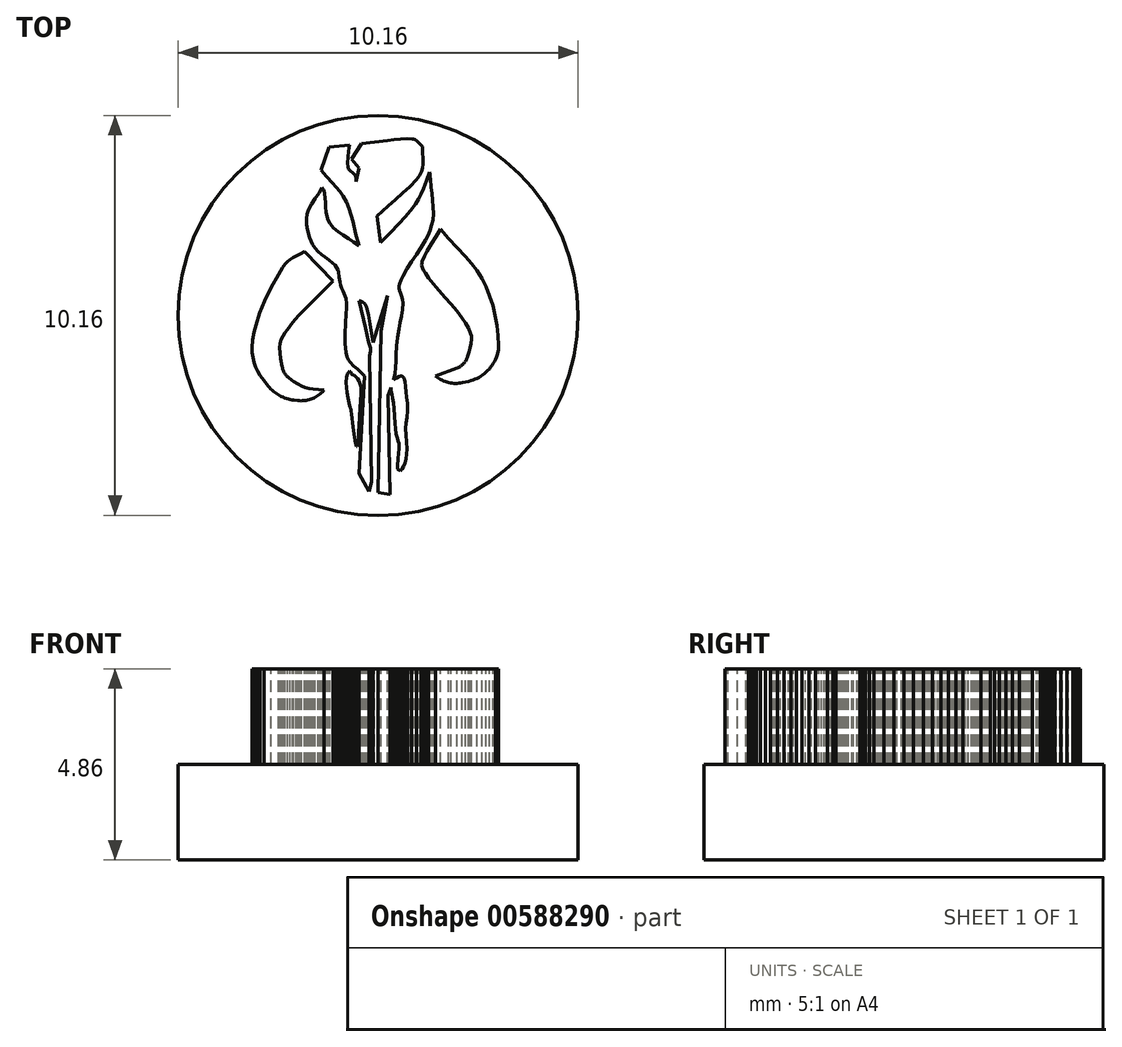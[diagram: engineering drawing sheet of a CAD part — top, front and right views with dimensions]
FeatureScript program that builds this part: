
annotation { "Feature Type Name" : "Feature", "Feature Type Description" : "" }
export const myFeature = defineFeature(function(context is Context, id is Id, definition is map)
    precondition{}
    {
        {
            var Q0;
            Q0=qCreatedBy(makeId("Top.planeOp"),FACE);
            var sketch = newSketch(context, id + "F0", { "sketchPlane" : qUnion([Q0])});
            skLineSegment(sketch, "E0", {"start": v(-3.17, -5.44) * mm, "end": v(-3.05, -5.48) * mm});
            skLineSegment(sketch, "E1", {"start": v(-3.05, -5.48) * mm, "end": v(-3, -5.51) * mm});
            skLineSegment(sketch, "E2", {"start": v(-3, -5.51) * mm, "end": v(-2.97, -5.54) * mm});
            skLineSegment(sketch, "E3", {"start": v(-2.97, -5.54) * mm, "end": v(-2.94, -5.6) * mm});
            skLineSegment(sketch, "E4", {"start": v(-2.94, -5.6) * mm, "end": v(-2.93, -5.66) * mm});
            skLineSegment(sketch, "E5", {"start": v(-2.93, -5.66) * mm, "end": v(-2.91, -5.76) * mm});
            skLineSegment(sketch, "E6", {"start": v(-2.91, -5.76) * mm, "end": v(-2.89, -5.81) * mm});
            skLineSegment(sketch, "E7", {"start": v(-2.89, -5.81) * mm, "end": v(-2.85, -5.86) * mm});
            skLineSegment(sketch, "E8", {"start": v(-2.85, -5.86) * mm, "end": v(-2.75, -5.91) * mm});
            skLineSegment(sketch, "E9", {"start": v(-2.75, -5.91) * mm, "end": v(-2.55, -5.98) * mm});
            skLineSegment(sketch, "E10", {"start": v(-2.55, -5.98) * mm, "end": v(-2.5, -6.01) * mm});
            skLineSegment(sketch, "E11", {"start": v(-2.5, -6.01) * mm, "end": v(-2.48, -6.03) * mm});
            skLineSegment(sketch, "E12", {"start": v(-2.48, -6.03) * mm, "end": v(-2.48, -6.03) * mm});
            skLineSegment(sketch, "E13", {"start": v(-2.48, -6.03) * mm, "end": v(-2.47, -6.04) * mm});
            skLineSegment(sketch, "E14", {"start": v(-2.47, -6.04) * mm, "end": v(-2.46, -6.05) * mm});
            skLineSegment(sketch, "E15", {"start": v(-2.46, -6.05) * mm, "end": v(-2.42, -6.08) * mm});
            skLineSegment(sketch, "E16", {"start": v(-2.42, -6.08) * mm, "end": v(-2.27, -6.23) * mm});
            skLineSegment(sketch, "E17", {"start": v(-2.27, -6.23) * mm, "end": v(-2, -6.56) * mm});
            skLineSegment(sketch, "E18", {"start": v(-2, -6.56) * mm, "end": v(-1.76, -6.92) * mm});
            skLineSegment(sketch, "E19", {"start": v(-1.76, -6.92) * mm, "end": v(-1.59, -7.32) * mm});
            skLineSegment(sketch, "E20", {"start": v(-1.59, -7.32) * mm, "end": v(-1.5, -7.74) * mm});
            skLineSegment(sketch, "E21", {"start": v(-1.5, -7.74) * mm, "end": v(-1.46, -8.75) * mm});
            skLineSegment(sketch, "E22", {"start": v(-1.46, -8.75) * mm, "end": v(-1.5, -9.75) * mm});
            skLineSegment(sketch, "E23", {"start": v(-1.5, -9.75) * mm, "end": v(-1.58, -10.76) * mm});
            skLineSegment(sketch, "E24", {"start": v(-1.58, -10.76) * mm, "end": v(-1.78, -13.47) * mm});
            skLineSegment(sketch, "E25", {"start": v(-1.78, -13.47) * mm, "end": v(-1.82, -14.2) * mm});
            skLineSegment(sketch, "E26", {"start": v(-1.82, -14.2) * mm, "end": v(-1.82, -14.94) * mm});
            skLineSegment(sketch, "E27", {"start": v(-1.82, -14.94) * mm, "end": v(-1.85, -15.67) * mm});
            skLineSegment(sketch, "E28", {"start": v(-1.85, -15.67) * mm, "end": v(-1.94, -16.21) * mm});
            skLineSegment(sketch, "E29", {"start": v(-1.94, -16.21) * mm, "end": v(-1.97, -16.33) * mm});
            skLineSegment(sketch, "E30", {"start": v(-1.97, -16.33) * mm, "end": v(-2.02, -16.45) * mm});
            skLineSegment(sketch, "E31", {"start": v(-2.02, -16.45) * mm, "end": v(-2.04, -16.47) * mm});
            skLineSegment(sketch, "E32", {"start": v(-2.04, -16.47) * mm, "end": v(-2.05, -16.47) * mm});
            skLineSegment(sketch, "E33", {"start": v(-2.05, -16.47) * mm, "end": v(-2.06, -16.47) * mm});
            skLineSegment(sketch, "E34", {"start": v(-2.06, -16.47) * mm, "end": v(-2.08, -16.47) * mm});
            skLineSegment(sketch, "E35", {"start": v(-2.08, -16.47) * mm, "end": v(-2.1, -16.46) * mm});
            skLineSegment(sketch, "E36", {"start": v(-2.1, -16.46) * mm, "end": v(-2.12, -16.43) * mm});
            skLineSegment(sketch, "E37", {"start": v(-2.12, -16.43) * mm, "end": v(-2.2, -16.26) * mm});
            skLineSegment(sketch, "E38", {"start": v(-2.2, -16.26) * mm, "end": v(-2.3, -15.9) * mm});
            skLineSegment(sketch, "E39", {"start": v(-2.3, -15.9) * mm, "end": v(-2.38, -15.55) * mm});
            skLineSegment(sketch, "E40", {"start": v(-2.38, -15.55) * mm, "end": v(-2.52, -14.6) * mm});
            skLineSegment(sketch, "E41", {"start": v(-2.52, -14.6) * mm, "end": v(-2.63, -13.64) * mm});
            skLineSegment(sketch, "E42", {"start": v(-2.63, -13.64) * mm, "end": v(-2.86, -11.73) * mm});
            skLineSegment(sketch, "E43", {"start": v(-2.86, -11.73) * mm, "end": v(-2.92, -11.25) * mm});
            skLineSegment(sketch, "E44", {"start": v(-2.92, -11.25) * mm, "end": v(-2.95, -11.02) * mm});
            skLineSegment(sketch, "E45", {"start": v(-2.95, -11.02) * mm, "end": v(-2.97, -10.9) * mm});
            skLineSegment(sketch, "E46", {"start": v(-2.97, -10.9) * mm, "end": v(-2.98, -10.88) * mm});
            skLineSegment(sketch, "E47", {"start": v(-2.98, -10.88) * mm, "end": v(-2.98, -10.87) * mm});
            skLineSegment(sketch, "E48", {"start": v(-2.98, -10.87) * mm, "end": v(-3.03, -10.84) * mm});
            skLineSegment(sketch, "E49", {"start": v(-3.03, -10.84) * mm, "end": v(-3.05, -10.82) * mm});
            skLineSegment(sketch, "E50", {"start": v(-3.05, -10.82) * mm, "end": v(-3.07, -10.8) * mm});
            skLineSegment(sketch, "E51", {"start": v(-3.07, -10.8) * mm, "end": v(-3.07, -10.8) * mm});
            skLineSegment(sketch, "E52", {"start": v(-3.07, -10.8) * mm, "end": v(-3.07, -10.77) * mm});
            skLineSegment(sketch, "E53", {"start": v(-3.07, -10.77) * mm, "end": v(-3.09, -10.7) * mm});
            skLineSegment(sketch, "E54", {"start": v(-3.09, -10.7) * mm, "end": v(-3.15, -10.43) * mm});
            skLineSegment(sketch, "E55", {"start": v(-3.15, -10.43) * mm, "end": v(-3.37, -9.34) * mm});
            skLineSegment(sketch, "E56", {"start": v(-3.37, -9.34) * mm, "end": v(-3.5, -8.6) * mm});
            skLineSegment(sketch, "E57", {"start": v(-3.5, -8.6) * mm, "end": v(-3.59, -7.84) * mm});
            skLineSegment(sketch, "E58", {"start": v(-3.59, -7.84) * mm, "end": v(-3.63, -7.09) * mm});
            skLineSegment(sketch, "E59", {"start": v(-3.63, -7.09) * mm, "end": v(-3.57, -6.34) * mm});
            skLineSegment(sketch, "E60", {"start": v(-3.57, -6.34) * mm, "end": v(-3.5, -6.07) * mm});
            skLineSegment(sketch, "E61", {"start": v(-3.5, -6.07) * mm, "end": v(-3.42, -5.81) * mm});
            skLineSegment(sketch, "E62", {"start": v(-3.42, -5.81) * mm, "end": v(-3.3, -5.61) * mm});
            skLineSegment(sketch, "E63", {"start": v(-3.3, -5.61) * mm, "end": v(-3.17, -5.44) * mm});
            skLineSegment(sketch, "E64", {"start": v(8.53, 23.62) * mm, "end": v(8.6, 23.33) * mm});
            skLineSegment(sketch, "E65", {"start": v(8.6, 23.33) * mm, "end": v(8.62, 23.18) * mm});
            skLineSegment(sketch, "E66", {"start": v(8.62, 23.18) * mm, "end": v(8.63, 23.03) * mm});
            skLineSegment(sketch, "E67", {"start": v(8.63, 23.03) * mm, "end": v(8.63, 23.03) * mm});
            skLineSegment(sketch, "E68", {"start": v(8.63, 23.03) * mm, "end": v(8.63, 23) * mm});
            skLineSegment(sketch, "E69", {"start": v(8.63, 23) * mm, "end": v(8.64, 22.93) * mm});
            skLineSegment(sketch, "E70", {"start": v(8.64, 22.93) * mm, "end": v(8.65, 22.63) * mm});
            skLineSegment(sketch, "E71", {"start": v(8.65, 22.63) * mm, "end": v(8.77, 21.44) * mm});
            skLineSegment(sketch, "E72", {"start": v(8.77, 21.44) * mm, "end": v(8.89, 20.48) * mm});
            skLineSegment(sketch, "E73", {"start": v(8.89, 20.48) * mm, "end": v(9, 19.52) * mm});
            skLineSegment(sketch, "E74", {"start": v(9, 19.52) * mm, "end": v(9.08, 18.56) * mm});
            skLineSegment(sketch, "E75", {"start": v(9.08, 18.56) * mm, "end": v(9.1, 17.6) * mm});
            skLineSegment(sketch, "E76", {"start": v(9.1, 17.6) * mm, "end": v(9.01, 16.64) * mm});
            skLineSegment(sketch, "E77", {"start": v(9.01, 16.64) * mm, "end": v(8.85, 15.87) * mm});
            skLineSegment(sketch, "E78", {"start": v(8.85, 15.87) * mm, "end": v(8.6, 15.12) * mm});
            skLineSegment(sketch, "E79", {"start": v(8.6, 15.12) * mm, "end": v(8.3, 14.38) * mm});
            skLineSegment(sketch, "E80", {"start": v(8.3, 14.38) * mm, "end": v(7.94, 13.68) * mm});
            skLineSegment(sketch, "E81", {"start": v(7.94, 13.68) * mm, "end": v(7.3, 12.62) * mm});
            skLineSegment(sketch, "E82", {"start": v(7.3, 12.62) * mm, "end": v(6.62, 11.6) * mm});
            skLineSegment(sketch, "E83", {"start": v(6.62, 11.6) * mm, "end": v(5.92, 10.57) * mm});
            skLineSegment(sketch, "E84", {"start": v(5.92, 10.57) * mm, "end": v(5.25, 9.53) * mm});
            skLineSegment(sketch, "E85", {"start": v(5.25, 9.53) * mm, "end": v(4.65, 8.45) * mm});
            skLineSegment(sketch, "E86", {"start": v(4.65, 8.45) * mm, "end": v(4.36, 7.86) * mm});
            skLineSegment(sketch, "E87", {"start": v(4.36, 7.86) * mm, "end": v(4.14, 7.24) * mm});
            skLineSegment(sketch, "E88", {"start": v(4.14, 7.24) * mm, "end": v(4.1, 6.96) * mm});
            skLineSegment(sketch, "E89", {"start": v(4.1, 6.96) * mm, "end": v(4.1, 6.68) * mm});
            skLineSegment(sketch, "E90", {"start": v(4.1, 6.68) * mm, "end": v(4.17, 6.31) * mm});
            skLineSegment(sketch, "E91", {"start": v(4.17, 6.31) * mm, "end": v(4.28, 5.96) * mm});
            skLineSegment(sketch, "E92", {"start": v(4.28, 5.96) * mm, "end": v(4.45, 5.49) * mm});
            skLineSegment(sketch, "E93", {"start": v(4.45, 5.49) * mm, "end": v(4.6, 5.02) * mm});
            skLineSegment(sketch, "E94", {"start": v(4.6, 5.02) * mm, "end": v(4.67, 4.53) * mm});
            skLineSegment(sketch, "E95", {"start": v(4.67, 4.53) * mm, "end": v(4.63, 3.56) * mm});
            skLineSegment(sketch, "E96", {"start": v(4.63, 3.56) * mm, "end": v(4.48, 2.6) * mm});
            skLineSegment(sketch, "E97", {"start": v(4.48, 2.6) * mm, "end": v(4.26, 1.63) * mm});
            skLineSegment(sketch, "E98", {"start": v(4.26, 1.63) * mm, "end": v(4.05, 0.68) * mm});
            skLineSegment(sketch, "E99", {"start": v(4.05, 0.68) * mm, "end": v(3.85, -0.55) * mm});
            skLineSegment(sketch, "E100", {"start": v(3.85, -0.55) * mm, "end": v(3.72, -1.78) * mm});
            skLineSegment(sketch, "E101", {"start": v(3.72, -1.78) * mm, "end": v(3.66, -3.03) * mm});
            skLineSegment(sketch, "E102", {"start": v(3.66, -3.03) * mm, "end": v(3.64, -3.96) * mm});
            skLineSegment(sketch, "E103", {"start": v(3.64, -3.96) * mm, "end": v(3.58, -4.9) * mm});
            skLineSegment(sketch, "E104", {"start": v(3.58, -4.9) * mm, "end": v(3.47, -5.82) * mm});
            skLineSegment(sketch, "E105", {"start": v(3.47, -5.82) * mm, "end": v(3.27, -6.73) * mm});
            skLineSegment(sketch, "E106", {"start": v(1.4, 13.3) * mm, "end": v(2.74, 14.74) * mm});
            skLineSegment(sketch, "E107", {"start": v(2.74, 14.74) * mm, "end": v(4.1, 16.14) * mm});
            skLineSegment(sketch, "E108", {"start": v(4.1, 16.14) * mm, "end": v(4.94, 17.05) * mm});
            skLineSegment(sketch, "E109", {"start": v(4.94, 17.05) * mm, "end": v(5.75, 18) * mm});
            skLineSegment(sketch, "E110", {"start": v(5.75, 18) * mm, "end": v(6.5, 18.98) * mm});
            skLineSegment(sketch, "E111", {"start": v(6.5, 18.98) * mm, "end": v(6.93, 19.69) * mm});
            skLineSegment(sketch, "E112", {"start": v(6.93, 19.69) * mm, "end": v(7.3, 20.44) * mm});
            skLineSegment(sketch, "E113", {"start": v(7.3, 20.44) * mm, "end": v(7.63, 21.22) * mm});
            skLineSegment(sketch, "E114", {"start": v(7.63, 21.22) * mm, "end": v(8.07, 22.43) * mm});
            skLineSegment(sketch, "E115", {"start": v(8.07, 22.43) * mm, "end": v(8.53, 23.62) * mm});
            skLineSegment(sketch, "E116", {"start": v(0.9, 17.17) * mm, "end": v(1.4, 13.3) * mm});
            skLineSegment(sketch, "E117", {"start": v(7.54, 27.39) * mm, "end": v(7.55, 26.52) * mm});
            skLineSegment(sketch, "E118", {"start": v(7.55, 26.52) * mm, "end": v(7.6, 25.64) * mm});
            skLineSegment(sketch, "E119", {"start": v(7.6, 25.64) * mm, "end": v(7.61, 24.77) * mm});
            skLineSegment(sketch, "E120", {"start": v(7.61, 24.77) * mm, "end": v(7.54, 24.23) * mm});
            skLineSegment(sketch, "E121", {"start": v(7.54, 24.23) * mm, "end": v(7.39, 23.72) * mm});
            skLineSegment(sketch, "E122", {"start": v(7.39, 23.72) * mm, "end": v(7.06, 23.12) * mm});
            skLineSegment(sketch, "E123", {"start": v(7.06, 23.12) * mm, "end": v(6.65, 22.57) * mm});
            skLineSegment(sketch, "E124", {"start": v(6.65, 22.57) * mm, "end": v(5.67, 21.53) * mm});
            skLineSegment(sketch, "E125", {"start": v(5.67, 21.53) * mm, "end": v(4.63, 20.55) * mm});
            skLineSegment(sketch, "E126", {"start": v(4.63, 20.55) * mm, "end": v(3.55, 19.6) * mm});
            skLineSegment(sketch, "E127", {"start": v(3.55, 19.6) * mm, "end": v(2.48, 18.64) * mm});
            skLineSegment(sketch, "E128", {"start": v(2.48, 18.64) * mm, "end": v(0.9, 17.17) * mm});
            skLineSegment(sketch, "E129", {"start": v(-1.38, 27.79) * mm, "end": v(0.5, 28.01) * mm});
            skLineSegment(sketch, "E130", {"start": v(0.5, 28.01) * mm, "end": v(2.4, 28.27) * mm});
            skLineSegment(sketch, "E131", {"start": v(2.4, 28.27) * mm, "end": v(3.34, 28.38) * mm});
            skLineSegment(sketch, "E132", {"start": v(3.34, 28.38) * mm, "end": v(4.29, 28.46) * mm});
            skLineSegment(sketch, "E133", {"start": v(4.29, 28.46) * mm, "end": v(5.23, 28.5) * mm});
            skLineSegment(sketch, "E134", {"start": v(5.23, 28.5) * mm, "end": v(5.99, 28.48) * mm});
            skLineSegment(sketch, "E135", {"start": v(5.99, 28.48) * mm, "end": v(6.2, 28.46) * mm});
            skLineSegment(sketch, "E136", {"start": v(6.2, 28.46) * mm, "end": v(6.39, 28.4) * mm});
            skLineSegment(sketch, "E137", {"start": v(6.39, 28.4) * mm, "end": v(6.6, 28.26) * mm});
            skLineSegment(sketch, "E138", {"start": v(6.6, 28.26) * mm, "end": v(6.8, 28.1) * mm});
            skLineSegment(sketch, "E139", {"start": v(6.8, 28.1) * mm, "end": v(7.16, 27.73) * mm});
            skLineSegment(sketch, "E140", {"start": v(7.16, 27.73) * mm, "end": v(7.54, 27.39) * mm});
            skLineSegment(sketch, "E141", {"start": v(-2.87, 25.5) * mm, "end": v(-1.38, 27.79) * mm});
            skLineSegment(sketch, "E142", {"start": v(-1.78, 24.22) * mm, "end": v(-2.87, 25.5) * mm});
            skLineSegment(sketch, "E143", {"start": v(-2.18, 22.23) * mm, "end": v(-1.78, 24.22) * mm});
            skLineSegment(sketch, "E144", {"start": v(-3.17, 27.59) * mm, "end": v(-3.27, 26.71) * mm});
            skLineSegment(sketch, "E145", {"start": v(-3.27, 26.71) * mm, "end": v(-3.39, 25.83) * mm});
            skLineSegment(sketch, "E146", {"start": v(-3.39, 25.83) * mm, "end": v(-3.44, 24.96) * mm});
            skLineSegment(sketch, "E147", {"start": v(-3.44, 24.96) * mm, "end": v(-3.38, 24.38) * mm});
            skLineSegment(sketch, "E148", {"start": v(-3.38, 24.38) * mm, "end": v(-3.27, 24.08) * mm});
            skLineSegment(sketch, "E149", {"start": v(-3.27, 24.08) * mm, "end": v(-3.15, 23.93) * mm});
            skLineSegment(sketch, "E150", {"start": v(-3.15, 23.93) * mm, "end": v(-3, 23.8) * mm});
            skLineSegment(sketch, "E151", {"start": v(-3, 23.8) * mm, "end": v(-2.68, 23.55) * mm});
            skLineSegment(sketch, "E152", {"start": v(-2.68, 23.55) * mm, "end": v(-2.38, 23.27) * mm});
            skLineSegment(sketch, "E153", {"start": v(-2.38, 23.27) * mm, "end": v(-2.24, 23.05) * mm});
            skLineSegment(sketch, "E154", {"start": v(-2.24, 23.05) * mm, "end": v(-2.19, 22.8) * mm});
            skLineSegment(sketch, "E155", {"start": v(-2.19, 22.8) * mm, "end": v(-2.19, 22.51) * mm});
            skLineSegment(sketch, "E156", {"start": v(-2.19, 22.51) * mm, "end": v(-2.18, 22.23) * mm});
            skLineSegment(sketch, "E157", {"start": v(-6.14, 27.3) * mm, "end": v(-3.17, 27.59) * mm});
            skLineSegment(sketch, "E158", {"start": v(-7.34, 23.92) * mm, "end": v(-6.14, 27.3) * mm});
            skLineSegment(sketch, "E159", {"start": v(-1.78, 12.9) * mm, "end": v(-2.23, 14.64) * mm});
            skLineSegment(sketch, "E160", {"start": v(-2.23, 14.64) * mm, "end": v(-2.65, 16.38) * mm});
            skLineSegment(sketch, "E161", {"start": v(-2.65, 16.38) * mm, "end": v(-2.91, 17.34) * mm});
            skLineSegment(sketch, "E162", {"start": v(-2.91, 17.34) * mm, "end": v(-3.22, 18.28) * mm});
            skLineSegment(sketch, "E163", {"start": v(-3.22, 18.28) * mm, "end": v(-3.6, 19.22) * mm});
            skLineSegment(sketch, "E164", {"start": v(-3.6, 19.22) * mm, "end": v(-4.08, 20.1) * mm});
            skLineSegment(sketch, "E165", {"start": v(-4.08, 20.1) * mm, "end": v(-4.55, 20.8) * mm});
            skLineSegment(sketch, "E166", {"start": v(-4.55, 20.8) * mm, "end": v(-5.08, 21.44) * mm});
            skLineSegment(sketch, "E167", {"start": v(-5.08, 21.44) * mm, "end": v(-5.64, 22.06) * mm});
            skLineSegment(sketch, "E168", {"start": v(-5.64, 22.06) * mm, "end": v(-6.5, 22.98) * mm});
            skLineSegment(sketch, "E169", {"start": v(-6.5, 22.98) * mm, "end": v(-7.34, 23.92) * mm});
            skLineSegment(sketch, "E170", {"start": v(-7.14, 21.34) * mm, "end": v(-6.97, 21.05) * mm});
            skLineSegment(sketch, "E171", {"start": v(-6.97, 21.05) * mm, "end": v(-6.89, 20.9) * mm});
            skLineSegment(sketch, "E172", {"start": v(-6.89, 20.9) * mm, "end": v(-6.86, 20.82) * mm});
            skLineSegment(sketch, "E173", {"start": v(-6.86, 20.82) * mm, "end": v(-6.85, 20.78) * mm});
            skLineSegment(sketch, "E174", {"start": v(-6.85, 20.78) * mm, "end": v(-6.84, 20.76) * mm});
            skLineSegment(sketch, "E175", {"start": v(-6.84, 20.76) * mm, "end": v(-6.84, 20.75) * mm});
            skLineSegment(sketch, "E176", {"start": v(-6.84, 20.75) * mm, "end": v(-6.84, 20.74) * mm});
            skLineSegment(sketch, "E177", {"start": v(-6.84, 20.74) * mm, "end": v(-6.84, 20.73) * mm});
            skLineSegment(sketch, "E178", {"start": v(-6.84, 20.73) * mm, "end": v(-6.83, 20.7) * mm});
            skLineSegment(sketch, "E179", {"start": v(-6.83, 20.7) * mm, "end": v(-6.8, 20.53) * mm});
            skLineSegment(sketch, "E180", {"start": v(-6.8, 20.53) * mm, "end": v(-6.72, 19.85) * mm});
            skLineSegment(sketch, "E181", {"start": v(-6.72, 19.85) * mm, "end": v(-6.68, 19.17) * mm});
            skLineSegment(sketch, "E182", {"start": v(-6.68, 19.17) * mm, "end": v(-6.65, 18.49) * mm});
            skLineSegment(sketch, "E183", {"start": v(-6.65, 18.49) * mm, "end": v(-6.58, 17.81) * mm});
            skLineSegment(sketch, "E184", {"start": v(-6.58, 17.81) * mm, "end": v(-6.46, 17.15) * mm});
            skLineSegment(sketch, "E185", {"start": v(-6.46, 17.15) * mm, "end": v(-6.26, 16.6) * mm});
            skLineSegment(sketch, "E186", {"start": v(-6.26, 16.6) * mm, "end": v(-5.98, 16.08) * mm});
            skLineSegment(sketch, "E187", {"start": v(-5.98, 16.08) * mm, "end": v(-5.46, 15.46) * mm});
            skLineSegment(sketch, "E188", {"start": v(-5.46, 15.46) * mm, "end": v(-4.85, 14.93) * mm});
            skLineSegment(sketch, "E189", {"start": v(-4.85, 14.93) * mm, "end": v(-4.1, 14.4) * mm});
            skLineSegment(sketch, "E190", {"start": v(-4.1, 14.4) * mm, "end": v(-3.32, 13.92) * mm});
            skLineSegment(sketch, "E191", {"start": v(-3.32, 13.92) * mm, "end": v(-2.54, 13.44) * mm});
            skLineSegment(sketch, "E192", {"start": v(-2.54, 13.44) * mm, "end": v(-1.78, 12.9) * mm});
            skLineSegment(sketch, "E193", {"start": v(-0.99, -6.13) * mm, "end": v(-1.48, -5.63) * mm});
            skLineSegment(sketch, "E194", {"start": v(-1.48, -5.63) * mm, "end": v(-2.01, -5.17) * mm});
            skLineSegment(sketch, "E195", {"start": v(-2.01, -5.17) * mm, "end": v(-2.56, -4.68) * mm});
            skLineSegment(sketch, "E196", {"start": v(-2.56, -4.68) * mm, "end": v(-3.06, -4.15) * mm});
            skLineSegment(sketch, "E197", {"start": v(-3.06, -4.15) * mm, "end": v(-3.3, -3.79) * mm});
            skLineSegment(sketch, "E198", {"start": v(-3.3, -3.79) * mm, "end": v(-3.5, -3.4) * mm});
            skLineSegment(sketch, "E199", {"start": v(-3.5, -3.4) * mm, "end": v(-3.67, -2.76) * mm});
            skLineSegment(sketch, "E200", {"start": v(-3.67, -2.76) * mm, "end": v(-3.76, -2.1) * mm});
            skLineSegment(sketch, "E201", {"start": v(-3.76, -2.1) * mm, "end": v(-3.8, -1.43) * mm});
            skLineSegment(sketch, "E202", {"start": v(-3.8, -1.43) * mm, "end": v(-3.81, 0.04) * mm});
            skLineSegment(sketch, "E203", {"start": v(-3.81, 0.04) * mm, "end": v(-3.73, 1.52) * mm});
            skLineSegment(sketch, "E204", {"start": v(-3.73, 1.52) * mm, "end": v(-3.64, 2.99) * mm});
            skLineSegment(sketch, "E205", {"start": v(-3.64, 2.99) * mm, "end": v(-3.61, 3.72) * mm});
            skLineSegment(sketch, "E206", {"start": v(-3.61, 3.72) * mm, "end": v(-3.61, 4.46) * mm});
            skLineSegment(sketch, "E207", {"start": v(-3.61, 4.46) * mm, "end": v(-3.68, 5.19) * mm});
            skLineSegment(sketch, "E208", {"start": v(-3.68, 5.19) * mm, "end": v(-3.77, 5.55) * mm});
            skLineSegment(sketch, "E209", {"start": v(-3.77, 5.55) * mm, "end": v(-3.92, 5.9) * mm});
            skLineSegment(sketch, "E210", {"start": v(-3.92, 5.9) * mm, "end": v(-4.1, 6.23) * mm});
            skLineSegment(sketch, "E211", {"start": v(-4.1, 6.23) * mm, "end": v(-4.3, 6.66) * mm});
            skLineSegment(sketch, "E212", {"start": v(-4.3, 6.66) * mm, "end": v(-4.46, 7.1) * mm});
            skLineSegment(sketch, "E213", {"start": v(-4.46, 7.1) * mm, "end": v(-4.57, 7.56) * mm});
            skLineSegment(sketch, "E214", {"start": v(-4.57, 7.56) * mm, "end": v(-4.64, 8.29) * mm});
            skLineSegment(sketch, "E215", {"start": v(-4.64, 8.29) * mm, "end": v(-4.75, 9.01) * mm});
            skLineSegment(sketch, "E216", {"start": v(-4.75, 9.01) * mm, "end": v(-4.85, 9.35) * mm});
            skLineSegment(sketch, "E217", {"start": v(-4.85, 9.35) * mm, "end": v(-5.01, 9.67) * mm});
            skLineSegment(sketch, "E218", {"start": v(-5.01, 9.67) * mm, "end": v(-5.3, 10.04) * mm});
            skLineSegment(sketch, "E219", {"start": v(-5.3, 10.04) * mm, "end": v(-5.63, 10.36) * mm});
            skLineSegment(sketch, "E220", {"start": v(-5.63, 10.36) * mm, "end": v(-6.16, 10.78) * mm});
            skLineSegment(sketch, "E221", {"start": v(-6.16, 10.78) * mm, "end": v(-6.7, 11.19) * mm});
            skLineSegment(sketch, "E222", {"start": v(-6.7, 11.19) * mm, "end": v(-7.24, 11.6) * mm});
            skLineSegment(sketch, "E223", {"start": v(-7.24, 11.6) * mm, "end": v(-7.74, 12.04) * mm});
            skLineSegment(sketch, "E224", {"start": v(-7.74, 12.04) * mm, "end": v(-8.18, 12.52) * mm});
            skLineSegment(sketch, "E225", {"start": v(-8.18, 12.52) * mm, "end": v(-8.54, 13.07) * mm});
            skLineSegment(sketch, "E226", {"start": v(-8.54, 13.07) * mm, "end": v(-8.99, 14.08) * mm});
            skLineSegment(sketch, "E227", {"start": v(-8.99, 14.08) * mm, "end": v(-9.3, 15.15) * mm});
            skLineSegment(sketch, "E228", {"start": v(-9.3, 15.15) * mm, "end": v(-9.43, 15.98) * mm});
            skLineSegment(sketch, "E229", {"start": v(-9.43, 15.98) * mm, "end": v(-9.44, 16.81) * mm});
            skLineSegment(sketch, "E230", {"start": v(-9.44, 16.81) * mm, "end": v(-9.33, 17.5) * mm});
            skLineSegment(sketch, "E231", {"start": v(-9.33, 17.5) * mm, "end": v(-9.11, 18.16) * mm});
            skLineSegment(sketch, "E232", {"start": v(-9.11, 18.16) * mm, "end": v(-8.68, 18.98) * mm});
            skLineSegment(sketch, "E233", {"start": v(-8.68, 18.98) * mm, "end": v(-8.16, 19.76) * mm});
            skLineSegment(sketch, "E234", {"start": v(-8.16, 19.76) * mm, "end": v(-7.62, 20.54) * mm});
            skLineSegment(sketch, "E235", {"start": v(-7.62, 20.54) * mm, "end": v(-7.14, 21.34) * mm});
            skLineSegment(sketch, "E236", {"start": v(-1.78, -20.42) * mm, "end": v(-0.99, -6.13) * mm});
            skLineSegment(sketch, "E237", {"start": v(-0.3, -23) * mm, "end": v(-1.78, -20.42) * mm});
            skLineSegment(sketch, "E238", {"start": v(0.1, -21.6) * mm, "end": v(-0.3, -23) * mm});
            skLineSegment(sketch, "E239", {"start": v(-0.2, -3.26) * mm, "end": v(0.1, -21.6) * mm});
            skLineSegment(sketch, "E240", {"start": v(-1.78, 4.88) * mm, "end": v(-0.83, 0.85) * mm});
            skLineSegment(sketch, "E241", {"start": v(-0.83, 0.85) * mm, "end": v(-0.6, -0.16) * mm});
            skLineSegment(sketch, "E242", {"start": v(-0.6, -0.16) * mm, "end": v(-0.35, -1.17) * mm});
            skLineSegment(sketch, "E243", {"start": v(-0.35, -1.17) * mm, "end": v(-0.22, -1.61) * mm});
            skLineSegment(sketch, "E244", {"start": v(-0.22, -1.61) * mm, "end": v(-0.1, -2.06) * mm});
            skLineSegment(sketch, "E245", {"start": v(-0.1, -2.06) * mm, "end": v(-0.08, -2.5) * mm});
            skLineSegment(sketch, "E246", {"start": v(-0.08, -2.5) * mm, "end": v(-0.2, -3.26) * mm});
            skLineSegment(sketch, "E247", {"start": v(0.3, -1.27) * mm, "end": v(0.1, 0.07) * mm});
            skLineSegment(sketch, "E248", {"start": v(0.1, 0.07) * mm, "end": v(-0.12, 1.41) * mm});
            skLineSegment(sketch, "E249", {"start": v(-0.12, 1.41) * mm, "end": v(-0.38, 2.75) * mm});
            skLineSegment(sketch, "E250", {"start": v(-0.38, 2.75) * mm, "end": v(-0.5, 3.33) * mm});
            skLineSegment(sketch, "E251", {"start": v(-0.5, 3.33) * mm, "end": v(-0.66, 3.9) * mm});
            skLineSegment(sketch, "E252", {"start": v(-0.66, 3.9) * mm, "end": v(-0.88, 4.37) * mm});
            skLineSegment(sketch, "E253", {"start": v(-0.88, 4.37) * mm, "end": v(-1.01, 4.52) * mm});
            skLineSegment(sketch, "E254", {"start": v(-1.01, 4.52) * mm, "end": v(-1.26, 4.66) * mm});
            skLineSegment(sketch, "E255", {"start": v(-1.26, 4.66) * mm, "end": v(-1.52, 4.76) * mm});
            skLineSegment(sketch, "E256", {"start": v(-1.52, 4.76) * mm, "end": v(-1.78, 4.88) * mm});
            skLineSegment(sketch, "E257", {"start": v(2.38, 5.57) * mm, "end": v(0.3, -1.27) * mm});
            skLineSegment(sketch, "E258", {"start": v(1.5, 0.41) * mm, "end": v(2.38, 5.57) * mm});
            skLineSegment(sketch, "E259", {"start": v(1, -23.2) * mm, "end": v(1.5, 0.41) * mm});
            skLineSegment(sketch, "E260", {"start": v(2.78, -23.5) * mm, "end": v(1, -23.2) * mm});
            skLineSegment(sketch, "E261", {"start": v(2.48, -9.01) * mm, "end": v(2.78, -23.5) * mm});
            skLineSegment(sketch, "E262", {"start": v(2.88, -7.87) * mm, "end": v(2.48, -9.01) * mm});
            skLineSegment(sketch, "E263", {"start": v(4.27, -20.02) * mm, "end": v(4.06, -19.87) * mm});
            skLineSegment(sketch, "E264", {"start": v(4.06, -19.87) * mm, "end": v(3.95, -19.79) * mm});
            skLineSegment(sketch, "E265", {"start": v(3.95, -19.79) * mm, "end": v(3.9, -19.72) * mm});
            skLineSegment(sketch, "E266", {"start": v(3.9, -19.72) * mm, "end": v(3.88, -19.65) * mm});
            skLineSegment(sketch, "E267", {"start": v(3.88, -19.65) * mm, "end": v(3.87, -19.64) * mm});
            skLineSegment(sketch, "E268", {"start": v(3.87, -19.64) * mm, "end": v(3.87, -19.63) * mm});
            skLineSegment(sketch, "E269", {"start": v(3.87, -19.63) * mm, "end": v(3.87, -19.62) * mm});
            skLineSegment(sketch, "E270", {"start": v(3.87, -19.62) * mm, "end": v(3.87, -19.62) * mm});
            skLineSegment(sketch, "E271", {"start": v(3.87, -19.62) * mm, "end": v(3.87, -19.6) * mm});
            skLineSegment(sketch, "E272", {"start": v(3.87, -19.6) * mm, "end": v(3.87, -19.54) * mm});
            skLineSegment(sketch, "E273", {"start": v(3.87, -19.54) * mm, "end": v(3.87, -19.27) * mm});
            skLineSegment(sketch, "E274", {"start": v(3.87, -19.27) * mm, "end": v(3.93, -18.2) * mm});
            skLineSegment(sketch, "E275", {"start": v(3.93, -18.2) * mm, "end": v(4.05, -16.76) * mm});
            skLineSegment(sketch, "E276", {"start": v(4.05, -16.76) * mm, "end": v(4.07, -16.39) * mm});
            skLineSegment(sketch, "E277", {"start": v(4.07, -16.39) * mm, "end": v(4.05, -16.03) * mm});
            skLineSegment(sketch, "E278", {"start": v(4.05, -16.03) * mm, "end": v(3.96, -15.67) * mm});
            skLineSegment(sketch, "E279", {"start": v(3.96, -15.67) * mm, "end": v(3.85, -15.32) * mm});
            skLineSegment(sketch, "E280", {"start": v(3.85, -15.32) * mm, "end": v(3.68, -14.6) * mm});
            skLineSegment(sketch, "E281", {"start": v(3.68, -14.6) * mm, "end": v(3.58, -13.85) * mm});
            skLineSegment(sketch, "E282", {"start": v(3.58, -13.85) * mm, "end": v(3.53, -13.1) * mm});
            skLineSegment(sketch, "E283", {"start": v(3.53, -13.1) * mm, "end": v(3.37, -10.89) * mm});
            skLineSegment(sketch, "E284", {"start": v(3.37, -10.89) * mm, "end": v(3.28, -10.13) * mm});
            skLineSegment(sketch, "E285", {"start": v(3.28, -10.13) * mm, "end": v(3.15, -9.38) * mm});
            skLineSegment(sketch, "E286", {"start": v(3.15, -9.38) * mm, "end": v(3.03, -8.88) * mm});
            skLineSegment(sketch, "E287", {"start": v(3.03, -8.88) * mm, "end": v(2.93, -8.38) * mm});
            skLineSegment(sketch, "E288", {"start": v(2.93, -8.38) * mm, "end": v(2.88, -7.87) * mm});
            skLineSegment(sketch, "E289", {"start": v(3.27, -6.73) * mm, "end": v(3.44, -6.62) * mm});
            skLineSegment(sketch, "E290", {"start": v(3.44, -6.62) * mm, "end": v(3.53, -6.56) * mm});
            skLineSegment(sketch, "E291", {"start": v(3.53, -6.56) * mm, "end": v(3.57, -6.53) * mm});
            skLineSegment(sketch, "E292", {"start": v(3.57, -6.53) * mm, "end": v(3.57, -6.53) * mm});
            skLineSegment(sketch, "E293", {"start": v(3.57, -6.53) * mm, "end": v(3.58, -6.53) * mm});
            skLineSegment(sketch, "E294", {"start": v(3.58, -6.53) * mm, "end": v(3.6, -6.51) * mm});
            skLineSegment(sketch, "E295", {"start": v(3.6, -6.51) * mm, "end": v(3.69, -6.45) * mm});
            skLineSegment(sketch, "E296", {"start": v(3.69, -6.45) * mm, "end": v(4.05, -6.25) * mm});
            skLineSegment(sketch, "E297", {"start": v(4.05, -6.25) * mm, "end": v(4.29, -6.18) * mm});
            skLineSegment(sketch, "E298", {"start": v(4.29, -6.18) * mm, "end": v(4.45, -6.18) * mm});
            skLineSegment(sketch, "E299", {"start": v(4.45, -6.18) * mm, "end": v(4.59, -6.22) * mm});
            skLineSegment(sketch, "E300", {"start": v(4.59, -6.22) * mm, "end": v(4.7, -6.3) * mm});
            skLineSegment(sketch, "E301", {"start": v(4.7, -6.3) * mm, "end": v(4.8, -6.48) * mm});
            skLineSegment(sketch, "E302", {"start": v(4.8, -6.48) * mm, "end": v(4.9, -6.72) * mm});
            skLineSegment(sketch, "E303", {"start": v(4.9, -6.72) * mm, "end": v(4.94, -6.97) * mm});
            skLineSegment(sketch, "E304", {"start": v(4.94, -6.97) * mm, "end": v(5.02, -7.72) * mm});
            skLineSegment(sketch, "E305", {"start": v(5.02, -7.72) * mm, "end": v(5.07, -8.46) * mm});
            skLineSegment(sketch, "E306", {"start": v(5.07, -8.46) * mm, "end": v(5.16, -9.2) * mm});
            skLineSegment(sketch, "E307", {"start": v(5.16, -9.2) * mm, "end": v(5.3, -10.2) * mm});
            skLineSegment(sketch, "E308", {"start": v(5.3, -10.2) * mm, "end": v(5.33, -11.22) * mm});
            skLineSegment(sketch, "E309", {"start": v(5.33, -11.22) * mm, "end": v(5.25, -12.23) * mm});
            skLineSegment(sketch, "E310", {"start": v(5.25, -12.23) * mm, "end": v(5.13, -13.02) * mm});
            skLineSegment(sketch, "E311", {"start": v(5.13, -13.02) * mm, "end": v(5.06, -13.8) * mm});
            skLineSegment(sketch, "E312", {"start": v(5.06, -13.8) * mm, "end": v(5.09, -14.81) * mm});
            skLineSegment(sketch, "E313", {"start": v(5.09, -14.81) * mm, "end": v(5.17, -15.82) * mm});
            skLineSegment(sketch, "E314", {"start": v(5.17, -15.82) * mm, "end": v(5.22, -16.82) * mm});
            skLineSegment(sketch, "E315", {"start": v(5.22, -16.82) * mm, "end": v(5.2, -17.56) * mm});
            skLineSegment(sketch, "E316", {"start": v(5.2, -17.56) * mm, "end": v(5.12, -18.29) * mm});
            skLineSegment(sketch, "E317", {"start": v(5.12, -18.29) * mm, "end": v(4.97, -18.86) * mm});
            skLineSegment(sketch, "E318", {"start": v(4.97, -18.86) * mm, "end": v(4.74, -19.4) * mm});
            skLineSegment(sketch, "E319", {"start": v(4.74, -19.4) * mm, "end": v(4.52, -19.72) * mm});
            skLineSegment(sketch, "E320", {"start": v(4.52, -19.72) * mm, "end": v(4.27, -20.02) * mm});
            skLineSegment(sketch, "E321", {"start": v(-9.72, 12.02) * mm, "end": v(-5.55, 7.75) * mm});
            skLineSegment(sketch, "E322", {"start": v(-15.04, -7.61) * mm, "end": v(-15.65, -6.85) * mm});
            skLineSegment(sketch, "E323", {"start": v(-15.65, -6.85) * mm, "end": v(-16.22, -6.06) * mm});
            skLineSegment(sketch, "E324", {"start": v(-16.22, -6.06) * mm, "end": v(-16.58, -5.46) * mm});
            skLineSegment(sketch, "E325", {"start": v(-16.58, -5.46) * mm, "end": v(-16.9, -4.83) * mm});
            skLineSegment(sketch, "E326", {"start": v(-16.9, -4.83) * mm, "end": v(-17.13, -4.16) * mm});
            skLineSegment(sketch, "E327", {"start": v(-17.13, -4.16) * mm, "end": v(-17.28, -3.45) * mm});
            skLineSegment(sketch, "E328", {"start": v(-17.28, -3.45) * mm, "end": v(-17.35, -2.72) * mm});
            skLineSegment(sketch, "E329", {"start": v(-17.35, -2.72) * mm, "end": v(-17.37, -1.98) * mm});
            skLineSegment(sketch, "E330", {"start": v(-17.37, -1.98) * mm, "end": v(-17.28, -0.87) * mm});
            skLineSegment(sketch, "E331", {"start": v(-17.28, -0.87) * mm, "end": v(-17.1, 0.23) * mm});
            skLineSegment(sketch, "E332", {"start": v(-17.1, 0.23) * mm, "end": v(-16.83, 1.31) * mm});
            skLineSegment(sketch, "E333", {"start": v(-16.83, 1.31) * mm, "end": v(-16.26, 3.08) * mm});
            skLineSegment(sketch, "E334", {"start": v(-16.26, 3.08) * mm, "end": v(-15.57, 4.8) * mm});
            skLineSegment(sketch, "E335", {"start": v(-15.57, 4.8) * mm, "end": v(-14.61, 6.76) * mm});
            skLineSegment(sketch, "E336", {"start": v(-14.61, 6.76) * mm, "end": v(-13.53, 8.65) * mm});
            skLineSegment(sketch, "E337", {"start": v(-13.53, 8.65) * mm, "end": v(-13.22, 9.16) * mm});
            skLineSegment(sketch, "E338", {"start": v(-13.22, 9.16) * mm, "end": v(-12.9, 9.68) * mm});
            skLineSegment(sketch, "E339", {"start": v(-12.9, 9.68) * mm, "end": v(-12.57, 10.16) * mm});
            skLineSegment(sketch, "E340", {"start": v(-12.57, 10.16) * mm, "end": v(-12.17, 10.6) * mm});
            skLineSegment(sketch, "E341", {"start": v(-12.17, 10.6) * mm, "end": v(-11.8, 10.9) * mm});
            skLineSegment(sketch, "E342", {"start": v(-11.8, 10.9) * mm, "end": v(-11.4, 11.14) * mm});
            skLineSegment(sketch, "E343", {"start": v(-11.4, 11.14) * mm, "end": v(-11, 11.35) * mm});
            skLineSegment(sketch, "E344", {"start": v(-11, 11.35) * mm, "end": v(-10.35, 11.66) * mm});
            skLineSegment(sketch, "E345", {"start": v(-10.35, 11.66) * mm, "end": v(-9.72, 12.02) * mm});
            skArc(sketch, "E346", {"start": v(-11.27, -9.7) * mm, "mid": v(-13.36, -9.02) * mm, "end": v(-15.04, -7.61) * mm});
            skLineSegment(sketch, "E347", {"start": v(-10.76, -9.75) * mm, "end": v(-11.27, -9.7) * mm});
            skArc(sketch, "E348", {"start": v(-7.1, -8.48) * mm, "mid": v(-8.79, -9.53) * mm, "end": v(-10.76, -9.75) * mm});
            skLineSegment(sketch, "E349", {"start": v(-6.84, -8.22) * mm, "end": v(-7.1, -8.48) * mm});
            skLineSegment(sketch, "E350", {"start": v(-11.97, -6.48) * mm, "end": v(-11.33, -6.93) * mm});
            skLineSegment(sketch, "E351", {"start": v(-11.33, -6.93) * mm, "end": v(-10.66, -7.36) * mm});
            skLineSegment(sketch, "E352", {"start": v(-10.66, -7.36) * mm, "end": v(-10.17, -7.61) * mm});
            skLineSegment(sketch, "E353", {"start": v(-10.17, -7.61) * mm, "end": v(-9.65, -7.81) * mm});
            skLineSegment(sketch, "E354", {"start": v(-9.65, -7.81) * mm, "end": v(-9.08, -7.95) * mm});
            skLineSegment(sketch, "E355", {"start": v(-9.08, -7.95) * mm, "end": v(-8.5, -8.04) * mm});
            skLineSegment(sketch, "E356", {"start": v(-8.5, -8.04) * mm, "end": v(-7.67, -8.12) * mm});
            skLineSegment(sketch, "E357", {"start": v(-7.67, -8.12) * mm, "end": v(-6.84, -8.22) * mm});
            skArc(sketch, "E358", {"start": v(-12.99, -4.8) * mm, "mid": v(-12.65, -5.74) * mm, "end": v(-11.97, -6.48) * mm});
            skLineSegment(sketch, "E359", {"start": v(-5.55, 7.75) * mm, "end": v(-6.92, 6.32) * mm});
            skLineSegment(sketch, "E360", {"start": v(-6.92, 6.32) * mm, "end": v(-8.34, 4.94) * mm});
            skLineSegment(sketch, "E361", {"start": v(-8.34, 4.94) * mm, "end": v(-9.74, 3.57) * mm});
            skLineSegment(sketch, "E362", {"start": v(-9.74, 3.57) * mm, "end": v(-10.62, 2.64) * mm});
            skLineSegment(sketch, "E363", {"start": v(-10.62, 2.64) * mm, "end": v(-11.46, 1.68) * mm});
            skLineSegment(sketch, "E364", {"start": v(-11.46, 1.68) * mm, "end": v(-12.23, 0.66) * mm});
            skLineSegment(sketch, "E365", {"start": v(-12.23, 0.66) * mm, "end": v(-12.55, 0.18) * mm});
            skLineSegment(sketch, "E366", {"start": v(-12.55, 0.18) * mm, "end": v(-12.86, -0.32) * mm});
            skLineSegment(sketch, "E367", {"start": v(-12.86, -0.32) * mm, "end": v(-13.11, -0.84) * mm});
            skLineSegment(sketch, "E368", {"start": v(-13.11, -0.84) * mm, "end": v(-13.28, -1.41) * mm});
            skLineSegment(sketch, "E369", {"start": v(-13.28, -1.41) * mm, "end": v(-13.34, -2.02) * mm});
            skLineSegment(sketch, "E370", {"start": v(-13.34, -2.02) * mm, "end": v(-13.3, -2.81) * mm});
            skLineSegment(sketch, "E371", {"start": v(-13.3, -2.81) * mm, "end": v(-13.2, -3.6) * mm});
            skLineSegment(sketch, "E372", {"start": v(-13.2, -3.6) * mm, "end": v(-12.99, -4.8) * mm});
            skLineSegment(sketch, "E373", {"start": v(9.52, -6.21) * mm, "end": v(9.43, -6.13) * mm});
            skArc(sketch, "E374", {"start": v(13.36, -7.13) * mm, "mid": v(11.33, -7.12) * mm, "end": v(9.52, -6.21) * mm});
            skLineSegment(sketch, "E375", {"start": v(14.25, -6.93) * mm, "end": v(13.36, -7.13) * mm});
            skArc(sketch, "E376", {"start": v(18.16, -3.77) * mm, "mid": v(16.57, -5.8) * mm, "end": v(14.25, -6.93) * mm});
            skLineSegment(sketch, "E377", {"start": v(10.12, 15.29) * mm, "end": v(11.31, 13.93) * mm});
            skLineSegment(sketch, "E378", {"start": v(11.31, 13.93) * mm, "end": v(12.55, 12.62) * mm});
            skLineSegment(sketch, "E379", {"start": v(12.55, 12.62) * mm, "end": v(13.76, 11.32) * mm});
            skLineSegment(sketch, "E380", {"start": v(13.76, 11.32) * mm, "end": v(14.64, 10.3) * mm});
            skLineSegment(sketch, "E381", {"start": v(14.64, 10.3) * mm, "end": v(15.45, 9.22) * mm});
            skLineSegment(sketch, "E382", {"start": v(15.45, 9.22) * mm, "end": v(16.17, 8.08) * mm});
            skLineSegment(sketch, "E383", {"start": v(16.17, 8.08) * mm, "end": v(16.79, 6.88) * mm});
            skLineSegment(sketch, "E384", {"start": v(16.79, 6.88) * mm, "end": v(17.33, 5.52) * mm});
            skLineSegment(sketch, "E385", {"start": v(17.33, 5.52) * mm, "end": v(17.78, 4.11) * mm});
            skLineSegment(sketch, "E386", {"start": v(17.78, 4.11) * mm, "end": v(18.14, 2.67) * mm});
            skLineSegment(sketch, "E387", {"start": v(18.14, 2.67) * mm, "end": v(18.4, 1.2) * mm});
            skLineSegment(sketch, "E388", {"start": v(18.4, 1.2) * mm, "end": v(18.56, -0.25) * mm});
            skLineSegment(sketch, "E389", {"start": v(18.56, -0.25) * mm, "end": v(18.65, -1.7) * mm});
            skLineSegment(sketch, "E390", {"start": v(18.65, -1.7) * mm, "end": v(18.61, -2.32) * mm});
            skLineSegment(sketch, "E391", {"start": v(18.61, -2.32) * mm, "end": v(18.48, -2.93) * mm});
            skLineSegment(sketch, "E392", {"start": v(18.48, -2.93) * mm, "end": v(18.33, -3.36) * mm});
            skLineSegment(sketch, "E393", {"start": v(18.33, -3.36) * mm, "end": v(18.16, -3.77) * mm});
            skLineSegment(sketch, "E394", {"start": v(14.08, -3.37) * mm, "end": v(14.1, -3.28) * mm});
            skLineSegment(sketch, "E395", {"start": v(14.1, -3.28) * mm, "end": v(14.3, -2.66) * mm});
            skLineSegment(sketch, "E396", {"start": v(14.3, -2.66) * mm, "end": v(14.48, -2.04) * mm});
            skLineSegment(sketch, "E397", {"start": v(14.48, -2.04) * mm, "end": v(14.63, -1.4) * mm});
            skLineSegment(sketch, "E398", {"start": v(14.63, -1.4) * mm, "end": v(14.68, -0.75) * mm});
            skLineSegment(sketch, "E399", {"start": v(14.68, -0.75) * mm, "end": v(14.64, -0.34) * mm});
            skLineSegment(sketch, "E400", {"start": v(14.64, -0.34) * mm, "end": v(14.54, 0.06) * mm});
            skLineSegment(sketch, "E401", {"start": v(14.54, 0.06) * mm, "end": v(14.2, 0.85) * mm});
            skLineSegment(sketch, "E402", {"start": v(14.2, 0.85) * mm, "end": v(13.78, 1.59) * mm});
            skLineSegment(sketch, "E403", {"start": v(13.78, 1.59) * mm, "end": v(13.3, 2.3) * mm});
            skLineSegment(sketch, "E404", {"start": v(13.3, 2.3) * mm, "end": v(12.52, 3.34) * mm});
            skLineSegment(sketch, "E405", {"start": v(12.52, 3.34) * mm, "end": v(11.67, 4.35) * mm});
            skLineSegment(sketch, "E406", {"start": v(11.67, 4.35) * mm, "end": v(10.8, 5.33) * mm});
            skLineSegment(sketch, "E407", {"start": v(10.8, 5.33) * mm, "end": v(9.49, 6.8) * mm});
            skLineSegment(sketch, "E408", {"start": v(9.49, 6.8) * mm, "end": v(8.42, 8.15) * mm});
            skLineSegment(sketch, "E409", {"start": v(8.42, 8.15) * mm, "end": v(7.93, 8.85) * mm});
            skLineSegment(sketch, "E410", {"start": v(7.93, 8.85) * mm, "end": v(7.7, 9.23) * mm});
            skLineSegment(sketch, "E411", {"start": v(7.7, 9.23) * mm, "end": v(7.5, 9.62) * mm});
            skLineSegment(sketch, "E412", {"start": v(7.5, 9.62) * mm, "end": v(7.44, 9.85) * mm});
            skLineSegment(sketch, "E413", {"start": v(7.44, 9.85) * mm, "end": v(7.4, 10.08) * mm});
            skLineSegment(sketch, "E414", {"start": v(7.4, 10.08) * mm, "end": v(7.42, 10.32) * mm});
            skLineSegment(sketch, "E415", {"start": v(7.42, 10.32) * mm, "end": v(7.48, 10.55) * mm});
            skLineSegment(sketch, "E416", {"start": v(7.48, 10.55) * mm, "end": v(7.79, 11.35) * mm});
            skLineSegment(sketch, "E417", {"start": v(7.79, 11.35) * mm, "end": v(8.18, 12.13) * mm});
            skLineSegment(sketch, "E418", {"start": v(8.18, 12.13) * mm, "end": v(8.81, 13.19) * mm});
            skLineSegment(sketch, "E419", {"start": v(8.81, 13.19) * mm, "end": v(9.48, 14.23) * mm});
            skLineSegment(sketch, "E420", {"start": v(9.48, 14.23) * mm, "end": v(10.12, 15.29) * mm});
            skArc(sketch, "E421", {"start": v(12.52, -5) * mm, "mid": v(13.49, -4.37) * mm, "end": v(14.08, -3.37) * mm});
            skLineSegment(sketch, "E422", {"start": v(9.43, -6.13) * mm, "end": v(12.52, -5) * mm});
            skArc(sketch, "E423", {"start": v(-19.3, -23.57) * mm, "mid": v(-19.28, -23.63) * mm, "end": v(-19.21, -23.66) * mm});
            skLineSegment(sketch, "E424", {"start": v(-19.3, -23.57) * mm, "end": v(-19.3, -23.57) * mm});
            skCircle(sketch, "E425", {"center": v(1.02, 2.68) * mm, "radius": 27.94 * mm});
            skPoint(sketch, "E425.first.point", {"position": v(-26.78, 5.93) * mm});
            skPoint(sketch, "E425.second.point", {"position": v(0, 31.06) * mm});
            skPoint(sketch, "E425.third.point", {"position": v(22.5, -14.72) * mm});
            skCircle(sketch, "E426", {"center": v(1.02, 2.68) * mm, "radius": 26.67 * mm});
            skCircle(sketch, "E427", {"center": v(1.02, 2.68) * mm, "radius": 29.21 * mm});
            skSolve(sketch);
        }
        {
            var Q0;
            Q0=makeQuery(id+"F0.imprint","IMPRINT",FACE,{"disambiguationData":[TD([[makeQuery(id+"F0.imprint","IMPRINT",EDGE,{"derivedFrom":sQuery(id+"F0.wireOp",EDGE,"E0")}),1.0]])]});
            var sketch = newSketch(context, id + "F1", { "sketchPlane" : qUnion([Q0])});
            skCircle(sketch, "E428.0", {"center": v(1.02, 2.68) * mm, "radius": 29.21 * mm});
            skSolve(sketch);
        }
        {
            var Q0;
            Q0=qSketchRegion(id+"F1",true);
            extrude(context, id + "F2", {"entities" : qUnion([Q0]), "oppositeDirection" : true, "depth" : 27.94 * mm, "offsetDistance" : 25.4 * mm});
        }
        {
            var Q0;
            Q0=makeQuery(id+"F0.imprint","IMPRINT",FACE,{"disambiguationData":[TD([[makeQuery(id+"F0.imprint","IMPRINT",EDGE,{"derivedFrom":sQuery(id+"F0.wireOp",EDGE,"E425")}),1.0]])]});
            var Q1;
            Q1=makeQuery(id+"F0.imprint","IMPRINT",FACE,{"disambiguationData":[TD([[makeQuery(id+"F0.imprint","IMPRINT",EDGE,{"derivedFrom":sQuery(id+"F0.wireOp",EDGE,"E0")}),1.0]])]});
            var Q2;
            Q2=makeQuery(id+"F0.imprint","IMPRINT",FACE,{"disambiguationData":[TD([[makeQuery(id+"F0.imprint","IMPRINT",EDGE,{"derivedFrom":sQuery(id+"F0.wireOp",EDGE,"E425")}),-1.0]])]});
            extrude(context, id + "F3", {"entities" : qUnion([Q0, Q1, Q2]), "operationType" : NewBodyOperationType.REMOVE, "oppositeDirection" : true, "depth" : 13.97 * mm, "offsetDistance" : 25.4 * mm});
        }
        {
            var Q0;
            Q0=makeQuery(id+"F2.opExtrude","SWEPT_BODY",BODY,{"disambiguationData":[OSD([sQuery(id+"F1.wireOp",EDGE,"E428.0")])]});
            var Q1;
            Q1=qCreatedBy(makeId("Origin.pointOp"),VERTEX);
            transform(context, id + "F4", {"entities" : qUnion([Q0]), "transformType" : TransformType.SCALE_UNIFORMLY, "scale" : .173913, "scalePoint" : qUnion([Q1]), "makeCopy" : false});
        }
    });
